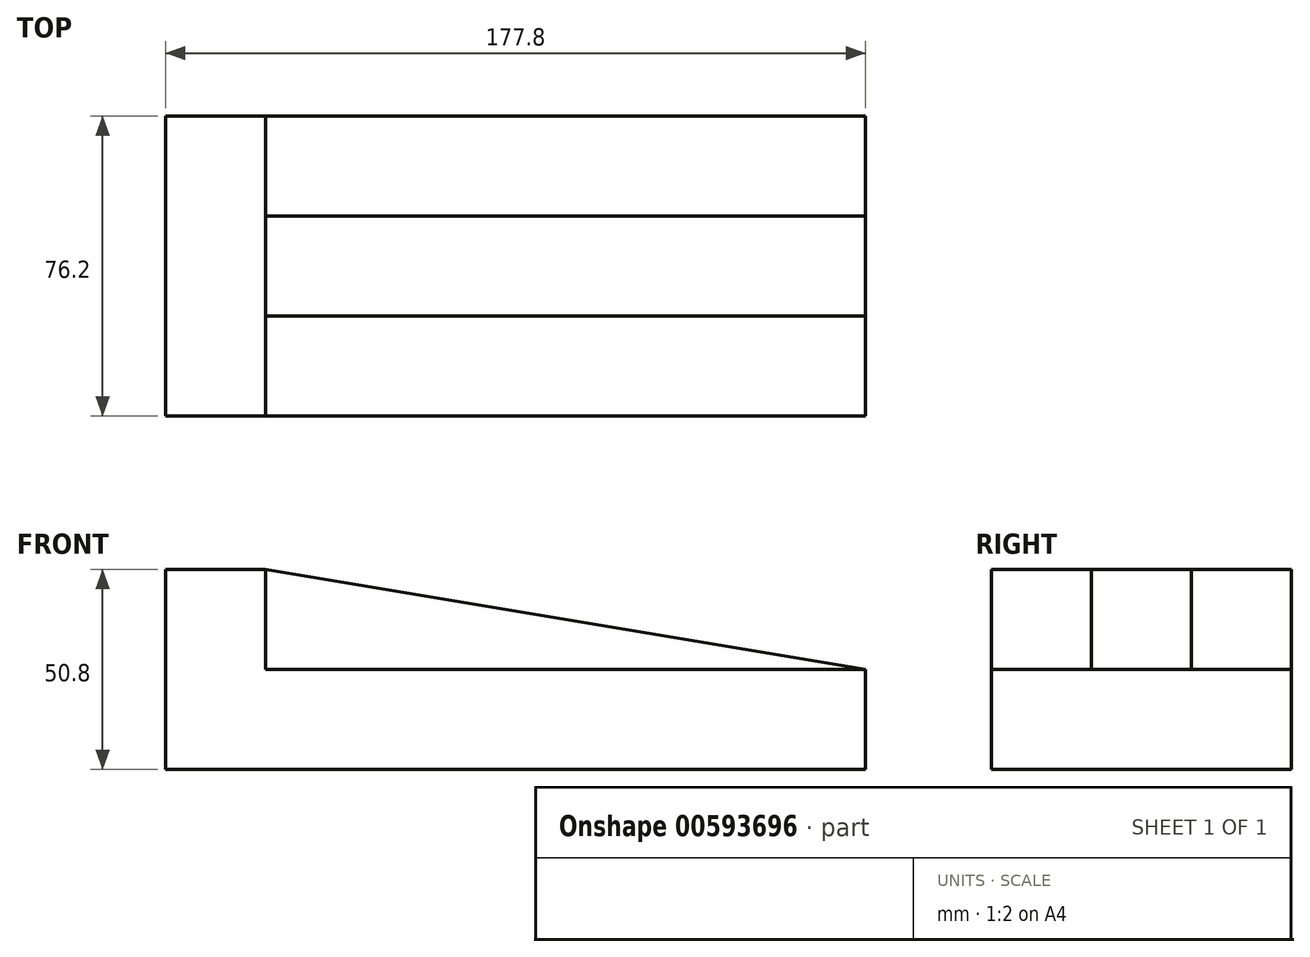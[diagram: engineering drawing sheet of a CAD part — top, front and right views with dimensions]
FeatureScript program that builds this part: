
annotation { "Feature Type Name" : "Feature", "Feature Type Description" : "" }
export const myFeature = defineFeature(function(context is Context, id is Id, definition is map)
    precondition{}
    {
        {
            var Q0;
            Q0=qCreatedBy(makeId("Front.planeOp"),FACE);
            var sketch = newSketch(context, id + "F0", { "sketchPlane" : qUnion([Q0])});
            skLineSegment(sketch, "E0", {"start": v(0, 0) * mm, "end": v(0, 50.8) * mm});
            skLineSegment(sketch, "E1", {"start": v(0, 50.8) * mm, "end": v(25.4, 50.8) * mm});
            skLineSegment(sketch, "E2", {"start": v(25.4, 50.8) * mm, "end": v(25.4, 25.4) * mm});
            skLineSegment(sketch, "E3", {"start": v(25.4, 25.4) * mm, "end": v(177.8, 25.4) * mm});
            skLineSegment(sketch, "E4", {"start": v(177.8, 25.4) * mm, "end": v(177.8, 0) * mm});
            skLineSegment(sketch, "E5", {"start": v(177.8, 0) * mm, "end": v(0, 0) * mm});
            skLineSegment(sketch, "E6", {"start": v(25.4, 50.8) * mm, "end": v(177.8, 25.4) * mm});
            skSolve(sketch);
        }
        {
            var Q0;
            Q0 = qSketchRegion(id + "F0", true);
            extrude(context, id + "F1", {"entities" : qUnion([Q0]), "oppositeDirection" : true, "depth" : 76.2 * mm, "offsetDistance" : 25.4 * mm});
        }
        {
            var Q0;
            Q0=makeQuery(id+"F1.opExtrude","CAP_FACE",FACE,{"disambiguationData":[OSD([sQuery(id+"F0.wireOp",EDGE,"E0"),sQuery(id+"F0.wireOp",EDGE,"E1"),sQuery(id+"F0.wireOp",EDGE,"E4"),sQuery(id+"F0.wireOp",EDGE,"E5"),sQuery(id+"F0.wireOp",EDGE,"E6")])],"isStart":true});
            var sketch = newSketch(context, id + "F2", { "sketchPlane" : qUnion([Q0])});
            skLineSegment(sketch, "E7", {"start": v(25.4, 50.8) * mm, "end": v(25.4, 25.4) * mm});
            skLineSegment(sketch, "E8", {"start": v(25.4, 25.4) * mm, "end": v(177.8, 25.4) * mm});
            skSolve(sketch);
        }
        {
            var Q0;
            Q0 = qSketchRegion(id + "F2", true);
            var Q1;
            Q1=makeQuery(id+"F2.imprint","IMPRINT",FACE,{"disambiguationData":[TD([[makeQuery(id+"F2.imprint","IMPRINT",EDGE,{"derivedFrom":sQuery(id+"F2.wireOp",EDGE,"E7")}),1.0]])]});
            extrude(context, id + "F3", {"entities" : qUnion([Q0, Q1]), "operationType" : NewBodyOperationType.REMOVE, "oppositeDirection" : true, "depth" : 25.4 * mm, "offsetDistance" : 25.4 * mm});
        }
        {
            var Q0;
            Q0=makeQuery(id+"F1.opExtrude","CAP_FACE",FACE,{"disambiguationData":[OSD([sQuery(id+"F0.wireOp",EDGE,"E0"),sQuery(id+"F0.wireOp",EDGE,"E1"),sQuery(id+"F0.wireOp",EDGE,"E4"),sQuery(id+"F0.wireOp",EDGE,"E5"),sQuery(id+"F0.wireOp",EDGE,"E6")])],"isStart":false});
            var sketch = newSketch(context, id + "F4", { "sketchPlane" : qUnion([Q0])});
            skLineSegment(sketch, "E9", {"start": v(-25.4, 50.8) * mm, "end": v(-25.4, 25.4) * mm});
            skLineSegment(sketch, "E10", {"start": v(-25.4, 25.4) * mm, "end": v(-177.8, 25.4) * mm});
            skSolve(sketch);
        }
        {
            var Q0;
            Q0 = qSketchRegion(id + "F4", true);
            var Q1;
            Q1=makeQuery(id+"F4.imprint","IMPRINT",FACE,{"disambiguationData":[TD([[makeQuery(id+"F4.imprint","IMPRINT",EDGE,{"derivedFrom":sQuery(id+"F4.wireOp",EDGE,"E9")}),-1.0]])]});
            extrude(context, id + "F5", {"entities" : qUnion([Q0, Q1]), "operationType" : NewBodyOperationType.REMOVE, "oppositeDirection" : true, "depth" : 25.4 * mm, "offsetDistance" : 25.4 * mm});
        }
    });
